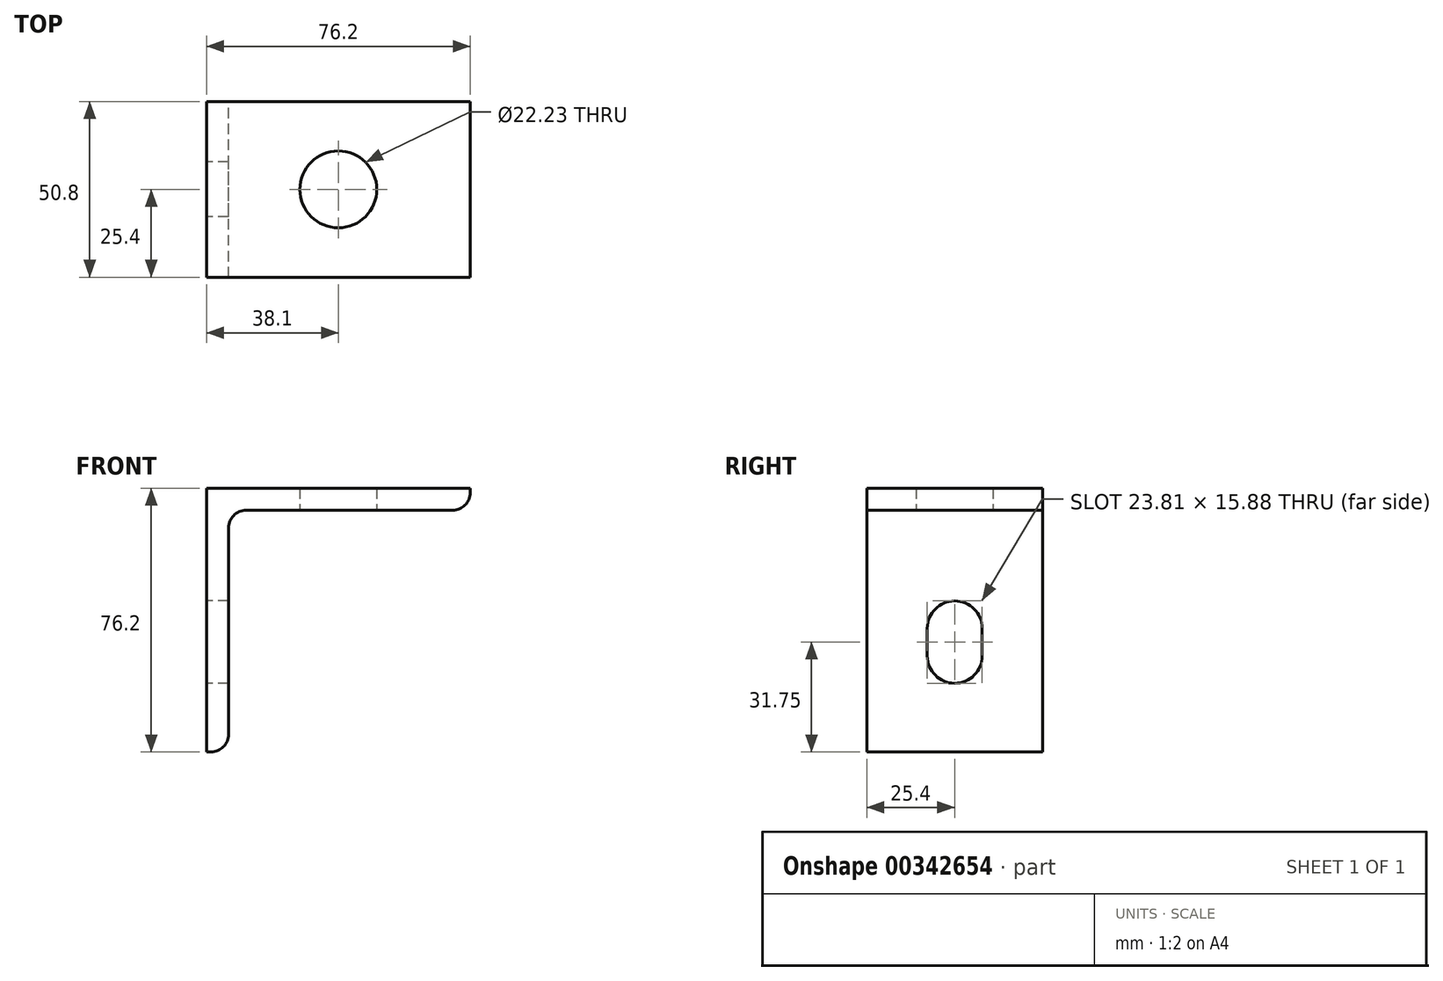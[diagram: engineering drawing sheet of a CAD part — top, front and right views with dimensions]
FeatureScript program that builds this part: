
annotation { "Feature Type Name" : "Feature", "Feature Type Description" : "" }
export const myFeature = defineFeature(function(context is Context, id is Id, definition is map)
    precondition{}
    {
        {
            var Q0;
            Q0=qCreatedBy(makeId("Front.planeOp"),FACE);
            var sketch = newSketch(context, id + "F0", { "sketchPlane" : qUnion([Q0])});
            skLineSegment(sketch, "E0", {"start": v(0, 0) * mm, "end": v(0, 76.2) * mm});
            skLineSegment(sketch, "E1", {"start": v(0, 76.2) * mm, "end": v(76.2, 76.2) * mm});
            skLineSegment(sketch, "E2", {"start": v(76.2, 76.2) * mm, "end": v(76.2, 69.85) * mm});
            skLineSegment(sketch, "E3", {"start": v(76.2, 69.85) * mm, "end": v(6.35, 69.85) * mm});
            skLineSegment(sketch, "E4", {"start": v(6.35, 69.85) * mm, "end": v(6.35, 0) * mm});
            skLineSegment(sketch, "E5", {"start": v(6.35, 0) * mm, "end": v(0, 0) * mm});
            skSolve(sketch);
        }
        {
            var Q0;
            Q0 = qSketchRegion(id + "F0", true);
            extrude(context, id + "F1", {"entities" : qUnion([Q0]), "depth" : 50.8 * mm});
        }
        {
            var Q0;
            Q0=qCreatedBy(makeId("Right.planeOp"),FACE);
            var sketch = newSketch(context, id + "F2", { "sketchPlane" : qUnion([Q0])});
            skArc(sketch, "E6", {"start": v(-33.34, 27.78) * mm, "mid": v(-25.4, 19.84) * mm, "end": v(-17.46, 27.78) * mm});
            skArc(sketch, "E7", {"start": v(-17.46, 35.72) * mm, "mid": v(-25.4, 43.66) * mm, "end": v(-33.34, 35.72) * mm});
            skLineSegment(sketch, "E8", {"start": v(-17.46, 35.72) * mm, "end": v(-17.46, 27.78) * mm});
            skLineSegment(sketch, "E9", {"start": v(-33.34, 35.72) * mm, "end": v(-33.34, 27.78) * mm});
            skLineSegment(sketch, "E10", {"start": v(-33.34, 31.75) * mm, "end": v(-17.46, 31.75) * mm});
            skSolve(sketch);
        }
        {
            var Q0;
            Q0 = qSketchRegion(id + "F2", true);
            extrude(context, id + "F3", {"entities" : qUnion([Q0]), "operationType" : NewBodyOperationType.REMOVE, "endBound" : BoundingType.THROUGH_ALL, "depth" : 25.4 * mm});
        }
        {
            var Q0;
            Q0=qCreatedBy(makeId("Top.planeOp"),FACE);
            var sketch = newSketch(context, id + "F4", { "sketchPlane" : qUnion([Q0])});
            skCircle(sketch, "E11", {"center": v(38.1, -25.4) * mm, "radius": 11.11 * mm});
            skSolve(sketch);
        }
        {
            var Q0;
            Q0 = qSketchRegion(id + "F4", true);
            var Q1;
            Q1=makeQuery(id+"F1.opExtrude","SWEPT_FACE",FACE,{"disambiguationData":[OSD([sQuery(id+"F0.wireOp",EDGE,"E1")])]});
            extrude(context, id + "F5", {"entities" : qUnion([Q0, Q1]), "operationType" : NewBodyOperationType.REMOVE, "endBound" : BoundingType.THROUGH_ALL, "depth" : 25.4 * mm});
        }
        {
            var Q0;
            Q0=makeQuery(id+"F1.opExtrude","SWEPT_EDGE",EDGE,{"disambiguationData":[OSD([sQuery(id+"F0.wireOp",EDGE,"E3"),sQuery(id+"F0.wireOp",EDGE,"E4")])]});
            var Q1;
            Q1=makeQuery(id+"F1.opExtrude","SWEPT_EDGE",EDGE,{"disambiguationData":[OSD([sQuery(id+"F0.wireOp",EDGE,"E2"),sQuery(id+"F0.wireOp",EDGE,"E3")])]});
            var Q2;
            Q2=makeQuery(id+"F1.opExtrude","SWEPT_EDGE",EDGE,{"disambiguationData":[OSD([sQuery(id+"F0.wireOp",EDGE,"E4"),sQuery(id+"F0.wireOp",EDGE,"E5")])]});
            fillet(context, id + "F6", {"entities" : qUnion([Q0, Q1, Q2]), "radius" : 5.08 * mm, "tangentPropagation" : true, "allowEdgeOverflow" : false});
        }
    });
